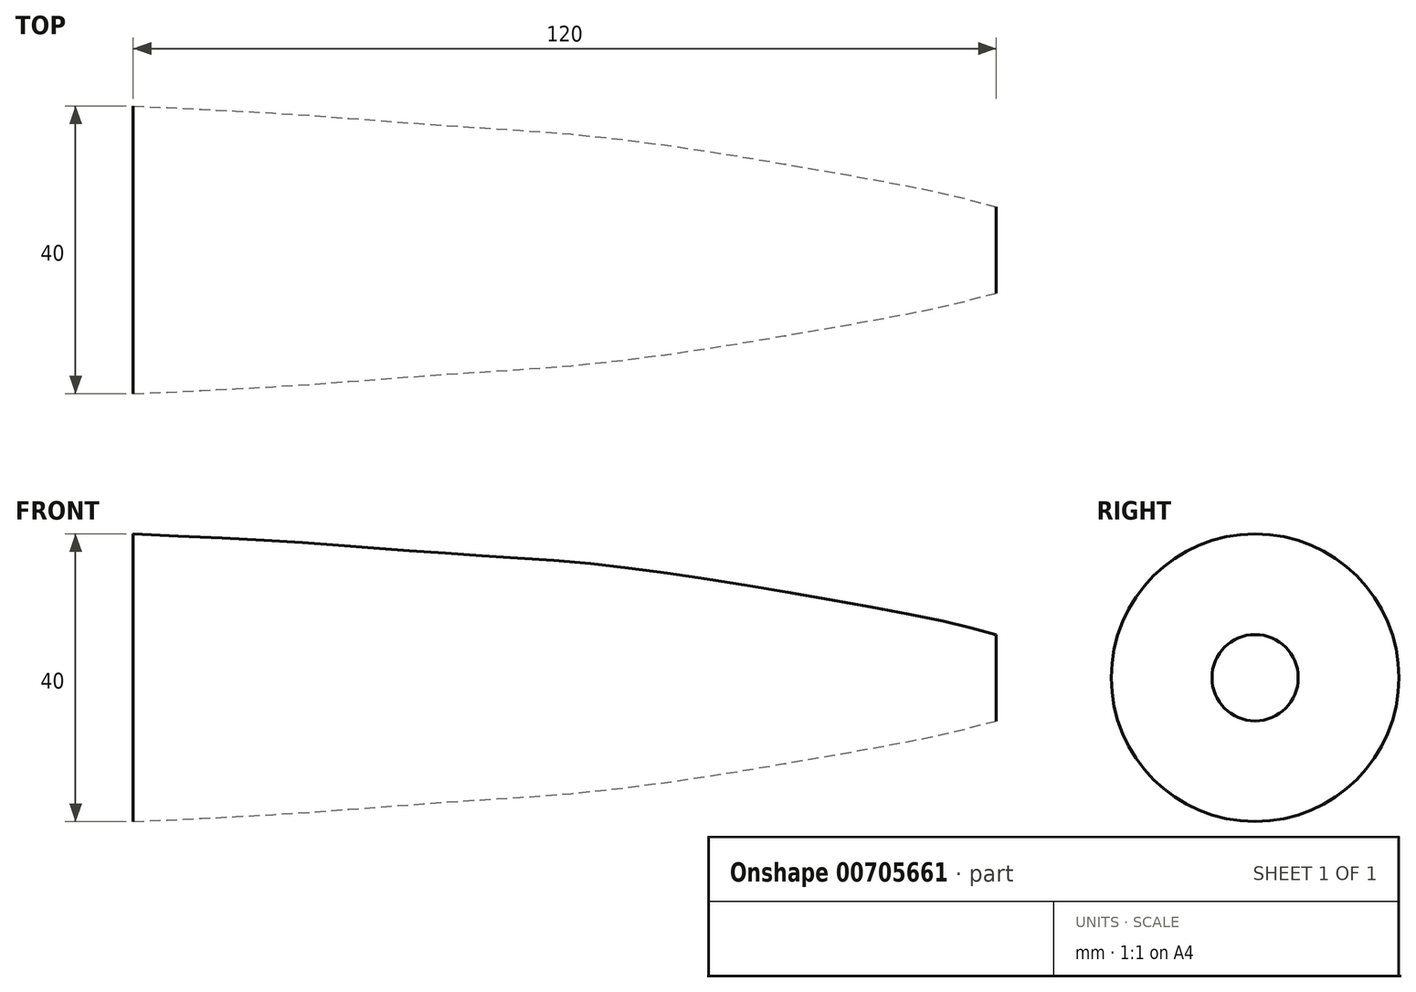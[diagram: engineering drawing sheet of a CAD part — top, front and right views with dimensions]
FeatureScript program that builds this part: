
annotation { "Feature Type Name" : "Feature", "Feature Type Description" : "" }
export const myFeature = defineFeature(function(context is Context, id is Id, definition is map)
    precondition{}
    {
        {
            var Q0;
            Q0=qCreatedBy(makeId("Front.planeOp"),FACE);
            var sketch = newSketch(context, id + "F0", { "sketchPlane" : qUnion([Q0])});
            skLineSegment(sketch, "E0", {"start": v(0, 0) * mm, "end": v(-120, 0) * mm, "construction": true});
            skLineSegment(sketch, "E1", {"start": v(0, 0) * mm, "end": v(0, 6) * mm});
            skLineSegment(sketch, "E2", {"start": v(-8, 0) * mm, "end": v(-8, 8) * mm, "construction": true});
            skLineSegment(sketch, "E3", {"start": v(-24, 0) * mm, "end": v(-24, 11) * mm, "construction": true});
            skLineSegment(sketch, "E4", {"start": v(-42, 0) * mm, "end": v(-42, 14) * mm, "construction": true});
            skLineSegment(sketch, "E5", {"start": v(-58, 0) * mm, "end": v(-58, 16) * mm, "construction": true});
            skLineSegment(sketch, "E6", {"start": v(-72, 0) * mm, "end": v(-72, 17) * mm, "construction": true});
            skLineSegment(sketch, "E7", {"start": v(-86, 0) * mm, "end": v(-86, 18) * mm, "construction": true});
            skLineSegment(sketch, "E8", {"start": v(-100, 0) * mm, "end": v(-100, 19) * mm, "construction": true});
            skLineSegment(sketch, "E9", {"start": v(-120, 0) * mm, "end": v(-120, 20) * mm});
            skFitSpline(sketch, "E10", {"points": [v(0, 6) * mm, v(-8, 8) * mm, v(-24, 11) * mm, v(-42, 14) * mm, v(-58, 16) * mm, v(-72, 17) * mm, v(-86, 18) * mm, v(-100, 19) * mm, v(-120, 20) * mm], "startDerivative": vector(-78.43, 21.2) * mm, "endDerivative": vector(-144.73, 6.55) * mm});
            skLineSegment(sketch, "E11", {"start": v(-120, 0) * mm, "end": v(0, 0) * mm});
            skSolve(sketch);
        }
        {
            var Q0;
            Q0=makeQuery(id+"F0.imprint","IMPRINT",FACE,{"disambiguationData":[TD([[makeQuery(id+"F0.imprint","IMPRINT",EDGE,{"derivedFrom":sQuery(id+"F0.wireOp",EDGE,"E1")}),1.0]])]});
            var Q1;
            Q1=sQuery(id+"F0.wireOp",EDGE,"E11");
            revolve(context, id + "F1", {"surfaceOperationType" : NewSurfaceOperationType.NEW, "entities" : qUnion([Q0]), "axis" : qUnion([Q1]), "revolveType" : RevolveType.FULL});
        }
    });
